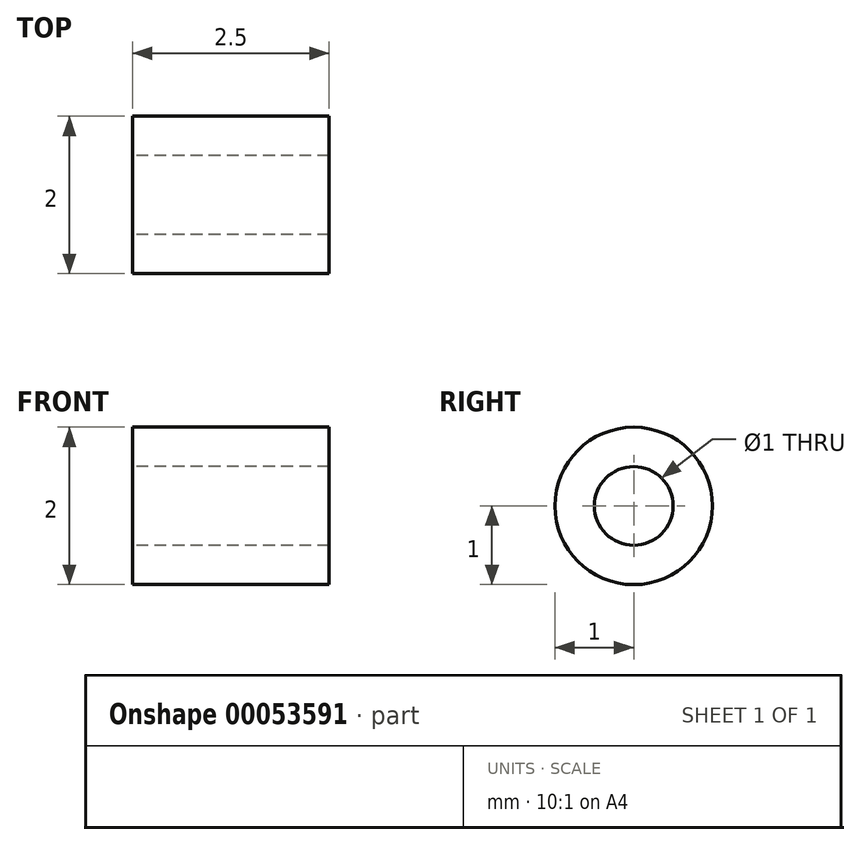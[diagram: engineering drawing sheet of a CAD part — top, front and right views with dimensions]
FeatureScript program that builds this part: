
annotation { "Feature Type Name" : "Feature", "Feature Type Description" : "" }
export const myFeature = defineFeature(function(context is Context, id is Id, definition is map)
    precondition{}
    {
        {
            var Q0;
            Q0=qCreatedBy(makeId("Right.planeOp"),FACE);
            var sketch = newSketch(context, id + "F0", { "sketchPlane" : qUnion([Q0])});
            skCircle(sketch, "E0", {"center": v(0, 0) * mm, "radius": 0.5 * mm});
            skCircle(sketch, "E1", {"center": v(0, 0) * mm, "radius": 1 * mm});
            skSolve(sketch);
        }
        {
            var Q0;
            Q0=makeQuery(id+"F0.imprint","IMPRINT",FACE,{"disambiguationData":[TD([[makeQuery(id+"F0.imprint","IMPRINT",EDGE,{"derivedFrom":sQuery(id+"F0.wireOp",EDGE,"E0")}),-1.0]])]});
            extrude(context, id + "F1", {"entities" : qUnion([Q0]), "depth" : 2.5 * mm});
        }
    });
